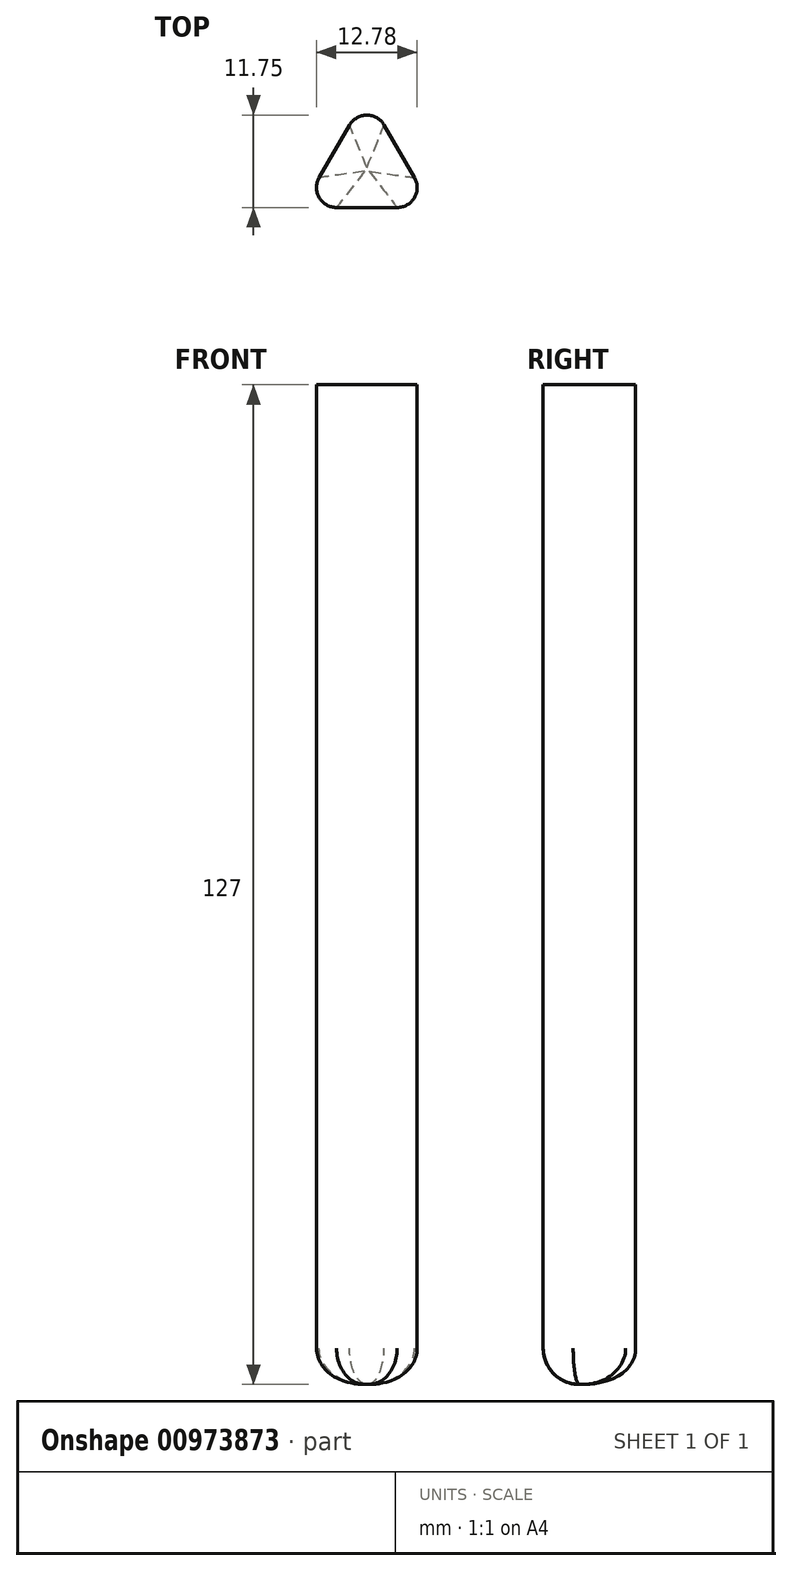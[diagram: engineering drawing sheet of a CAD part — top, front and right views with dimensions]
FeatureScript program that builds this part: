
annotation { "Feature Type Name" : "Feature", "Feature Type Description" : "" }
export const myFeature = defineFeature(function(context is Context, id is Id, definition is map)
    precondition{}
    {
        {
            var Q0;
            Q0=qCreatedBy(makeId("Top.planeOp"),FACE);
            var sketch = newSketch(context, id + "F0", { "sketchPlane" : qUnion([Q0])});
            skLineSegment(sketch, "E0.0", {"start": v(3.85, -2.72) * mm, "end": v(-3.85, -2.72) * mm});
            skLineSegment(sketch, "E0.1", {"start": v(-6.05, 1.1) * mm, "end": v(-2.2, 7.76) * mm});
            skLineSegment(sketch, "E0.2", {"start": v(2.2, 7.76) * mm, "end": v(6.05, 1.1) * mm});
            skPoint(sketch, "E0.0.midPoint", {"position": v(0, -2.72) * mm});
            skPoint(sketch, "E1.visualSharp", {"position": v(0, 11.57) * mm});
            skArc(sketch, "E1.filletArc", {"start": v(2.2, 7.76) * mm, "mid": v(0, 9.03) * mm, "end": v(-2.2, 7.76) * mm});
            skPoint(sketch, "E2.visualSharp", {"position": v(8.25, -2.72) * mm});
            skArc(sketch, "E2.filletArc", {"start": v(3.85, -2.72) * mm, "mid": v(6.05, -1.45) * mm, "end": v(6.05, 1.1) * mm});
            skPoint(sketch, "E3.visualSharp", {"position": v(-8.25, -2.72) * mm});
            skArc(sketch, "E3.filletArc", {"start": v(-6.05, 1.1) * mm, "mid": v(-6.05, -1.45) * mm, "end": v(-3.85, -2.72) * mm});
            skSolve(sketch);
        }
        {
            var Q0;
            Q0=makeQuery(id+"F0.imprint","IMPRINT",FACE,{"disambiguationData":[TD([[makeQuery(id+"F0.imprint","IMPRINT",EDGE,{"derivedFrom":sQuery(id+"F0.wireOp",EDGE,"E0.0")}),-1.0]])]});
            extrude(context, id + "F1", {"entities" : qUnion([Q0]), "depth" : 127 * mm, "offsetDistance" : 25.4 * mm});
        }
        {
            var Q0;
            Q0=makeQuery(id+"F1.opExtrude","CAP_FACE",FACE,{"disambiguationData":[OSD([sQuery(id+"F0.wireOp",EDGE,"E0.0"),sQuery(id+"F0.wireOp",EDGE,"E0.1"),sQuery(id+"F0.wireOp",EDGE,"E0.2"),sQuery(id+"F0.wireOp",EDGE,"E1.filletArc"),sQuery(id+"F0.wireOp",EDGE,"E2.filletArc"),sQuery(id+"F0.wireOp",EDGE,"E3.filletArc")])],"isStart":true});
            var Q1;
            Q1=makeQuery(id+"F1.opExtrude","CAP_EDGE",EDGE,{"disambiguationData":[OSD([sQuery(id+"F0.wireOp",EDGE,"E2.filletArc")])],"isStart":true});
            var Q2;
            Q2=makeQuery(id+"F1.opExtrude","CAP_EDGE",EDGE,{"disambiguationData":[OSD([sQuery(id+"F0.wireOp",EDGE,"E1.filletArc")])],"isStart":true});
            var Q3;
            Q3=makeQuery(id+"F1.opExtrude","CAP_EDGE",EDGE,{"disambiguationData":[OSD([sQuery(id+"F0.wireOp",EDGE,"E0.1")])],"isStart":true});
            var Q4;
            Q4=makeQuery(id+"F1.opExtrude","CAP_EDGE",EDGE,{"disambiguationData":[OSD([sQuery(id+"F0.wireOp",EDGE,"E3.filletArc")])],"isStart":true});
            var Q5;
            Q5=makeQuery(id+"F1.opExtrude","CAP_EDGE",EDGE,{"disambiguationData":[OSD([sQuery(id+"F0.wireOp",EDGE,"E0.2")])],"isStart":true});
            fillet(context, id + "F2", {"entities" : qUnion([Q0, Q1, Q2, Q3, Q4, Q5]), "radius" : 4.6 * mm, "tangentPropagation" : true, "allowEdgeOverflow" : false});
        }
    });
